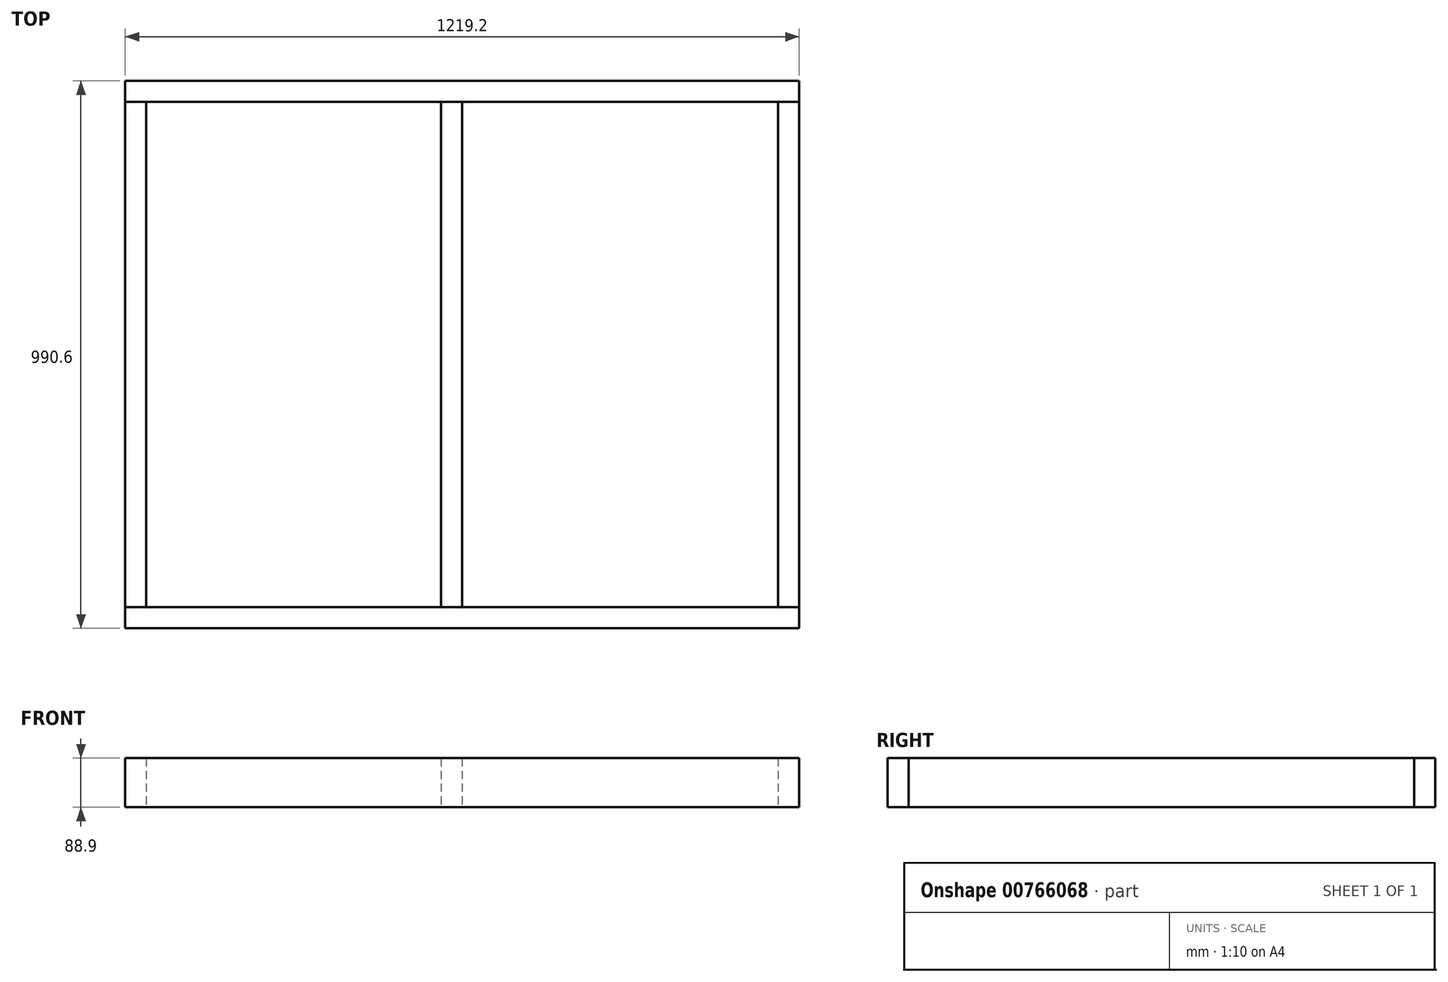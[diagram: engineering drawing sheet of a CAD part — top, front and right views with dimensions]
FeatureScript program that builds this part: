
annotation { "Feature Type Name" : "Feature", "Feature Type Description" : "" }
export const myFeature = defineFeature(function(context is Context, id is Id, definition is map)
    precondition{}
    {
        {
            var Q0;
            Q0=qCreatedBy(makeId("Front.planeOp"),FACE);
            var sketch = newSketch(context, id + "F0", { "sketchPlane" : qUnion([Q0])});
            skLineSegment(sketch, "E0.bottom", {"start": v(-629.04, 88.9) * mm, "end": v(590.16, 88.9) * mm});
            skLineSegment(sketch, "E0.top", {"start": v(-629.04, 0) * mm, "end": v(590.16, 0) * mm});
            skLineSegment(sketch, "E0.left", {"start": v(-629.04, 88.9) * mm, "end": v(-629.04, 0) * mm});
            skLineSegment(sketch, "E0.right", {"start": v(590.16, 88.9) * mm, "end": v(590.16, 0) * mm});
            skSolve(sketch);
        }
        {
            var Q0;
            Q0=qSketchRegion(id+"F0",true);
            extrude(context, id + "F1", {"entities" : qUnion([Q0]), "oppositeDirection" : true, "depth" : 38.1 * mm, "offsetDistance" : 25.4 * mm});
        }
        {
            var Q0;
            Q0=qCreatedBy(makeId("Top.planeOp"),FACE);
            var sketch = newSketch(context, id + "F2", { "sketchPlane" : qUnion([Q0])});
            skLineSegment(sketch, "E1.bottom", {"start": v(-629.04, 38.1) * mm, "end": v(-590.94, 38.1) * mm});
            skLineSegment(sketch, "E1.top", {"start": v(-629.04, 952.5) * mm, "end": v(-590.94, 952.5) * mm});
            skLineSegment(sketch, "E1.left", {"start": v(-629.04, 38.1) * mm, "end": v(-629.04, 952.5) * mm});
            skLineSegment(sketch, "E1.right", {"start": v(-590.94, 38.1) * mm, "end": v(-590.94, 952.5) * mm});
            skLineSegment(sketch, "E2.bottom", {"start": v(552.06, 38.1) * mm, "end": v(590.16, 38.1) * mm});
            skLineSegment(sketch, "E2.top", {"start": v(552.06, 952.5) * mm, "end": v(590.16, 952.5) * mm});
            skLineSegment(sketch, "E2.left", {"start": v(552.06, 38.1) * mm, "end": v(552.06, 952.5) * mm});
            skLineSegment(sketch, "E2.right", {"start": v(590.16, 38.1) * mm, "end": v(590.16, 952.5) * mm});
            skLineSegment(sketch, "E3.bottom", {"start": v(-57.54, 38.1) * mm, "end": v(-19.44, 38.1) * mm});
            skLineSegment(sketch, "E3.top", {"start": v(-57.54, 952.5) * mm, "end": v(-19.44, 952.5) * mm});
            skLineSegment(sketch, "E3.left", {"start": v(-57.54, 38.1) * mm, "end": v(-57.54, 952.5) * mm});
            skLineSegment(sketch, "E3.right", {"start": v(-19.44, 38.1) * mm, "end": v(-19.44, 952.5) * mm});
            skSolve(sketch);
        }
        {
            var Q0;
            Q0=qSketchRegion(id+"F2",true);
            extrude(context, id + "F3", {"entities" : qUnion([Q0]), "depth" : 88.9 * mm, "offsetDistance" : 25.4 * mm});
        }
        {
            var Q0;
            Q0=qCreatedBy(makeId("Top.planeOp"),FACE);
            var sketch = newSketch(context, id + "F4", { "sketchPlane" : qUnion([Q0])});
            skLineSegment(sketch, "E4.bottom", {"start": v(-629.04, 990.6) * mm, "end": v(590.16, 990.6) * mm});
            skLineSegment(sketch, "E4.top", {"start": v(-629.04, 952.5) * mm, "end": v(590.16, 952.5) * mm});
            skLineSegment(sketch, "E4.left", {"start": v(-629.04, 990.6) * mm, "end": v(-629.04, 952.5) * mm});
            skLineSegment(sketch, "E4.right", {"start": v(590.16, 990.6) * mm, "end": v(590.16, 952.5) * mm});
            skSolve(sketch);
        }
        {
            var Q0;
            Q0=qSketchRegion(id+"F4",true);
            extrude(context, id + "F5", {"entities" : qUnion([Q0]), "depth" : 88.9 * mm, "offsetDistance" : 25.4 * mm});
        }
    });
